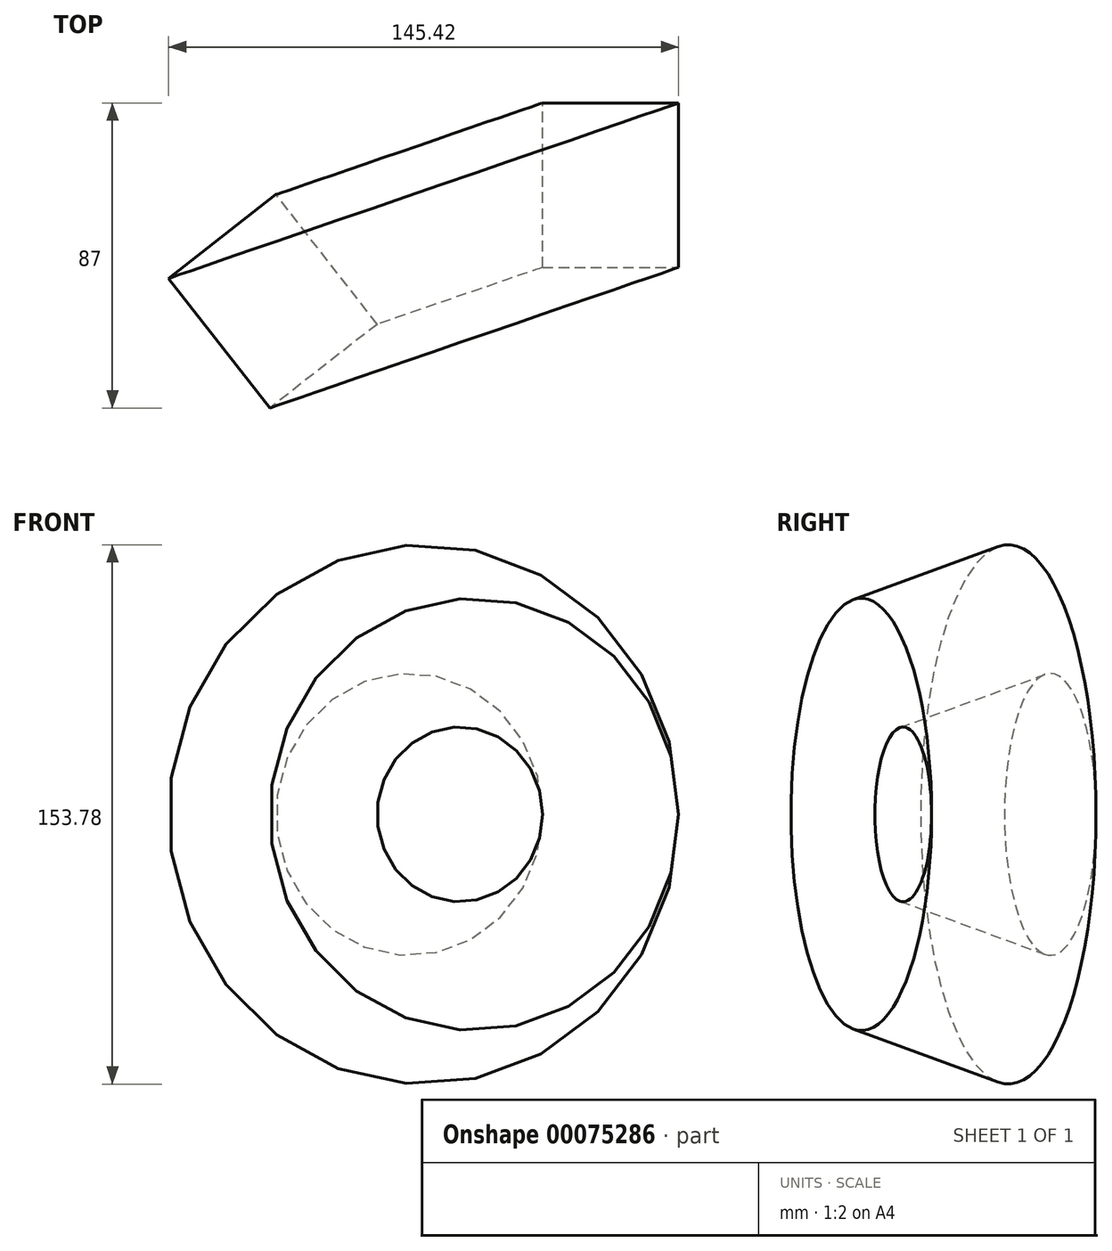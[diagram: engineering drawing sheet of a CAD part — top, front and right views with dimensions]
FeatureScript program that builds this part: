
annotation { "Feature Type Name" : "Feature", "Feature Type Description" : "" }
export const myFeature = defineFeature(function(context is Context, id is Id, definition is map)
    precondition{}
    {
        {
            var Q0;
            Q0=qCreatedBy(makeId("Top.planeOp"),FACE);
            var sketch = newSketch(context, id + "F0", { "sketchPlane" : qUnion([Q0])});
            skLineSegment(sketch, "E0.bottom", {"start": v(0, 0) * mm, "end": v(38.83, 0) * mm});
            skLineSegment(sketch, "E0.top", {"start": v(0, 46.9) * mm, "end": v(38.83, 46.9) * mm});
            skLineSegment(sketch, "E0.left", {"start": v(0, 0) * mm, "end": v(0, 46.9) * mm});
            skLineSegment(sketch, "E0.right", {"start": v(38.83, 0) * mm, "end": v(38.83, 46.9) * mm});
            skLineSegment(sketch, "E1", {"start": v(-19.34, -20.4) * mm, "end": v(-44.5, 52.73) * mm, "construction": true});
            skSolve(sketch);
        }
        {
            var Q0;
            Q0 = qSketchRegion(id + "F0", true);
            var Q1;
            Q1=sQuery(id+"F0.wireOp",EDGE,"E1");
            revolve(context, id + "F1", {"entities" : qUnion([Q0]), "axis" : qUnion([Q1]), "revolveType" : RevolveType.FULL});
        }
    });
